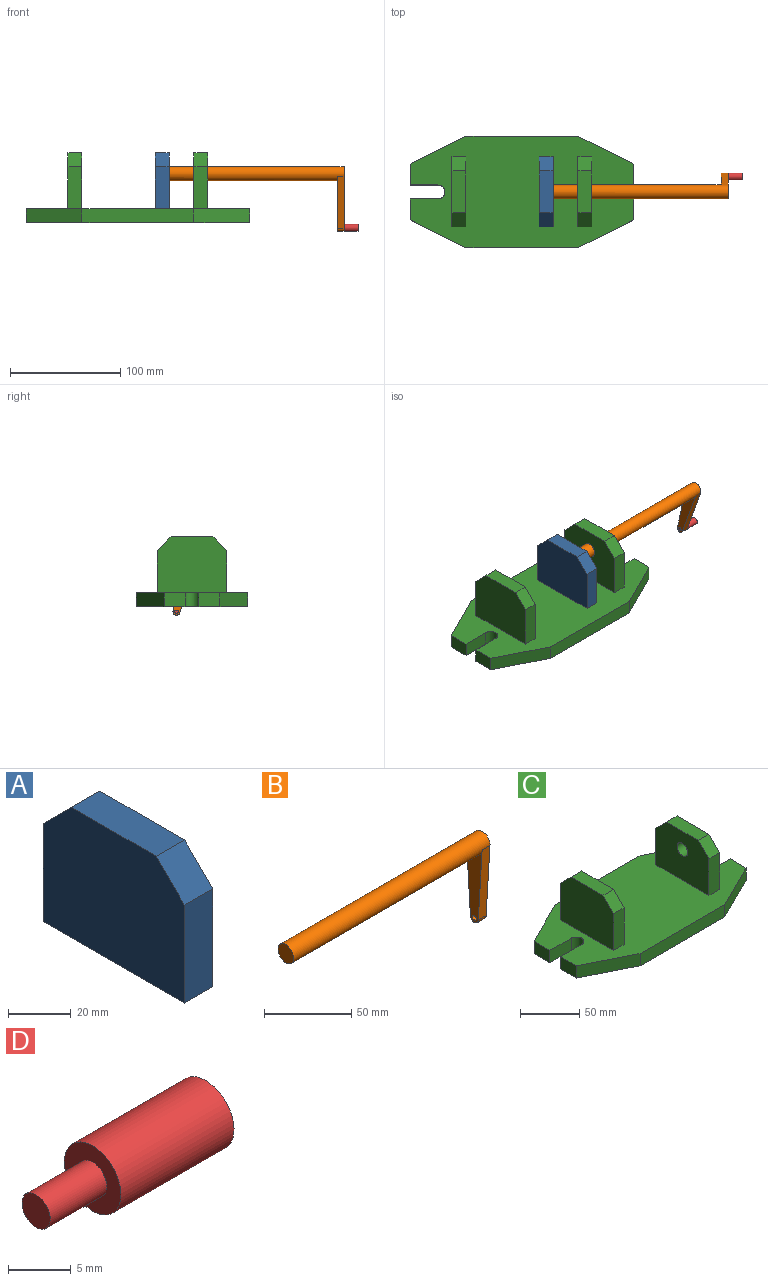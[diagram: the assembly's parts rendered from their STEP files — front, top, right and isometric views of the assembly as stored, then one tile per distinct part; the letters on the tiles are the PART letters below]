
ASSEMBLY  parts=4 mates=6
PART A: 8 faces, bbox 12.7x63.5x50.8 mm
  f0: plane 38.1x12.7mm, normal (0,1,0), area 483.9mm2, adj f1,f3,f5,f6
  f1: plane 63.5x50.8mm, normal (-1,0,0), area 3064.5mm2, adj f0,f2,f4,f5,f6,f7
  f2: plane 38.1x12.7mm, normal (0,-1,0), area 483.9mm2, adj f1,f3,f5,f7
  f3: plane 63.5x50.8mm, normal (1,0,0), area 3064.5mm2, adj f0,f2,f4,f5,f6,f7
  f4: plane 38.1x12.7mm, normal (0,0,1), area 483.9mm2, adj f1,f3,f6,f7
  f5: plane 63.5x12.7mm, normal (0,0,-1), area 806.5mm2, adj f0,f1,f2,f3
  f6: plane 12.7x12.7mm, normal (0,0.71,0.71), area 228.1mm2, adj f0,f1,f3,f4
  f7: plane 12.7x12.7mm, normal (0,-0.71,0.71), area 228.1mm2, adj f1,f2,f3,f4
PART B: 10 faces, bbox 158.8x12.7x60.6 mm
  f0: cylinder r=6.35mm len=158.75mm, axis (-1,0,0), area 6212.2mm2, adj f1,f2,f6,f7,f9
  f1: plane 12.7x12.7mm, normal (-1,0,0), area 126.7mm2, adj f0
  f2: plane 53.87x12.68mm, normal (-1,0,0), area 431.8mm2, adj f0,f3,f4,f5,f6,f7,f8
  f3: plane 6.35x0.01mm, normal (0,0,-1), area 0mm2, adj f2,f4,f7,f9
  f4: cylinder r=3.17mm len=6.35mm, axis (-1,0,0), area 63.2mm2, adj f2,f3,f5,f9
  f5: plane 6.35x0.01mm, normal (0,0,-1), area 0mm2, adj f2,f4,f6,f9
  f6: plane 50.7x6.35mm, normal (0,1,-0.06), area 322.6mm2, adj f0,f2,f5,f9
  f7: plane 50.7x6.35mm, normal (0,-1,-0.06), area 322.6mm2, adj f0,f2,f3,f9
  f8: cylinder r=1.59mm len=6.35mm, axis (-1,0,0), area 63.3mm2, adj f2,f9
  f9: plane 60.62x12.7mm, normal (1,0,0), area 558.5mm2, adj f0,f3,f4,f5,f6,f7,f8
PART C: 33 faces, bbox 203.2x101.6x63.5 mm
  f0: plane 203.2x101.6mm, normal (0,0,1), area 15679.7mm2, adj f1,f2,f3,f4,f5,f6,f8,f9
  f1: plane 101.6x12.7mm, normal (0,1,0), area 1290.3mm2, adj f0,f7,f15,f16
  f2: plane 19.05x12.7mm, normal (-1,0,0), area 241.9mm2, adj f0,f7,f10,f15
  f3: plane 19.05x12.7mm, normal (-1,0,0), area 241.9mm2, adj f0,f7,f9,f14
  f4: plane 101.6x12.7mm, normal (0,-1,0), area 1290.3mm2, adj f0,f7,f14,f17
  f5: plane 19.05x12.7mm, normal (1,0,0), area 241.9mm2, adj f0,f7,f11,f16
  f6: plane 19.05x12.7mm, normal (1,0,0), area 241.9mm2, adj f0,f7,f13,f17
  f7: plane 203.2x101.6mm, normal (0,0,-1), area 17292.6mm2, adj f1,f2,f3,f4,f5,f6,f8,f9
  f8: cylinder r=6.35mm len=12.7mm, axis (0,0,1), area 253.4mm2, adj f0,f7,f9,f10
  f9: plane 25.4x12.7mm, normal (0,1,0), area 322.6mm2, adj f0,f3,f7,f8
  f10: plane 25.4x12.7mm, normal (0,-1,0), area 322.6mm2, adj f0,f2,f7,f8
  f11: plane 25.4x12.7mm, normal (0,-1,0), area 322.6mm2, adj f0,f5,f7,f12
  f12: cylinder r=6.35mm len=12.7mm, axis (0,0,1), area 253.4mm2, adj f0,f7,f11,f13
  f13: plane 25.4x12.7mm, normal (0,1,0), area 322.6mm2, adj f0,f6,f7,f12
  f14: plane 50.8x25.4mm, normal (-0.45,-0.89,0), area 721.3mm2, adj f0,f3,f4,f7
  f15: plane 50.8x25.4mm, normal (-0.45,0.89,0), area 721.3mm2, adj f0,f1,f2,f7
  f16: plane 50.8x25.4mm, normal (0.45,0.89,0), area 721.3mm2, adj f0,f1,f5,f7
  f17: plane 50.8x25.4mm, normal (0.45,-0.89,0), area 721.3mm2, adj f0,f4,f6,f7
  f18: plane 38.1x12.7mm, normal (0,1,0), area 483.9mm2, adj f0,f19,f21,f30
  f19: plane 63.5x50.8mm, normal (-1,0,0), area 3064.5mm2, adj f0,f18,f20,f22,f30,f31
  f20: plane 38.1x12.7mm, normal (0,-1,0), area 483.9mm2, adj f0,f19,f21,f31
  f21: plane 63.5x50.8mm, normal (1,0,0), area 3064.5mm2, adj f0,f18,f20,f22,f30,f31
  f22: plane 38.1x12.7mm, normal (0,0,1), area 483.9mm2, adj f19,f21,f30,f31
  f23: plane 38.1x12.7mm, normal (0,1,0), area 483.9mm2, adj f0,f24,f26,f28
  f24: plane 63.5x50.8mm, normal (-1,0,0), area 2937.8mm2, adj f0,f23,f25,f27,f28,f29,f32
  f25: plane 38.1x12.7mm, normal (0,-1,0), area 483.9mm2, adj f0,f24,f26,f29
  f26: plane 63.5x50.8mm, normal (1,0,0), area 2937.8mm2, adj f0,f23,f25,f27,f28,f29,f32
  f27: plane 38.1x12.7mm, normal (0,0,1), area 483.9mm2, adj f24,f26,f28,f29
  f28: plane 12.7x12.7mm, normal (0,0.71,0.71), area 228.1mm2, adj f23,f24,f26,f27
  f29: plane 12.7x12.7mm, normal (0,-0.71,0.71), area 228.1mm2, adj f24,f25,f26,f27
  f30: plane 12.7x12.7mm, normal (0,0.71,0.71), area 228.1mm2, adj f18,f19,f21,f22
  f31: plane 12.7x12.7mm, normal (0,-0.71,0.71), area 228.1mm2, adj f19,f20,f21,f22
  f32: cylinder r=6.35mm len=12.7mm, axis (1,0,0), area 506.7mm2, adj f24,f26
PART D: 5 faces, bbox 19.1x6.4x6.4 mm
  f0: cylinder r=1.59mm len=6.35mm, axis (1,0,0), area 63.3mm2, adj f1,f4
  f1: plane 3.18x3.18mm, normal (-1,0,0), area 7.9mm2, adj f0
  f2: cylinder r=3.17mm len=12.7mm, axis (-1,0,0), area 253.4mm2, adj f3,f4
  f3: plane 6.35x6.35mm, normal (1,0,0), area 31.7mm2, adj f2
  f4: plane 6.35x6.35mm, normal (-1,0,0), area 23.8mm2, adj f0,f2
PLACE A t=(-48.38,-3.3,13.81)mm
PLACE B rot(axis=(1,0,0),16deg) t=(-48.38,8.96,15.53)mm
PLACE C t=(-38.71,-3.3,13.81)mm fixed
PLACE D rot(axis=(-1,0,0),108.3deg) t=(-48.38,17.11,7.06)mm
MATE planar A.f3 <-> B.f0  axis (1,0,0) through (-10.28,-3.3,50.79)mm
MATE planar C.f0 <-> A.f5  axis (0,0,1) through (-38.71,-3.3,26.51)mm
MATE planar C.f20 <-> A.f2  axis (0,-1,0) through (-95.86,-35.05,45.56)mm
MATE planar D.f0 <-> B.f9  axis (-1,0,0) through (148.47,10.8,9.14)mm
MATE cylindrical D.f0 <-> B.f4  axis (1,0,0) through (145.3,10.8,9.14)mm
MATE cylindrical B.f0 <-> C.f32  axis (-1,0,0) through (69.1,-3.3,58.26)mm
